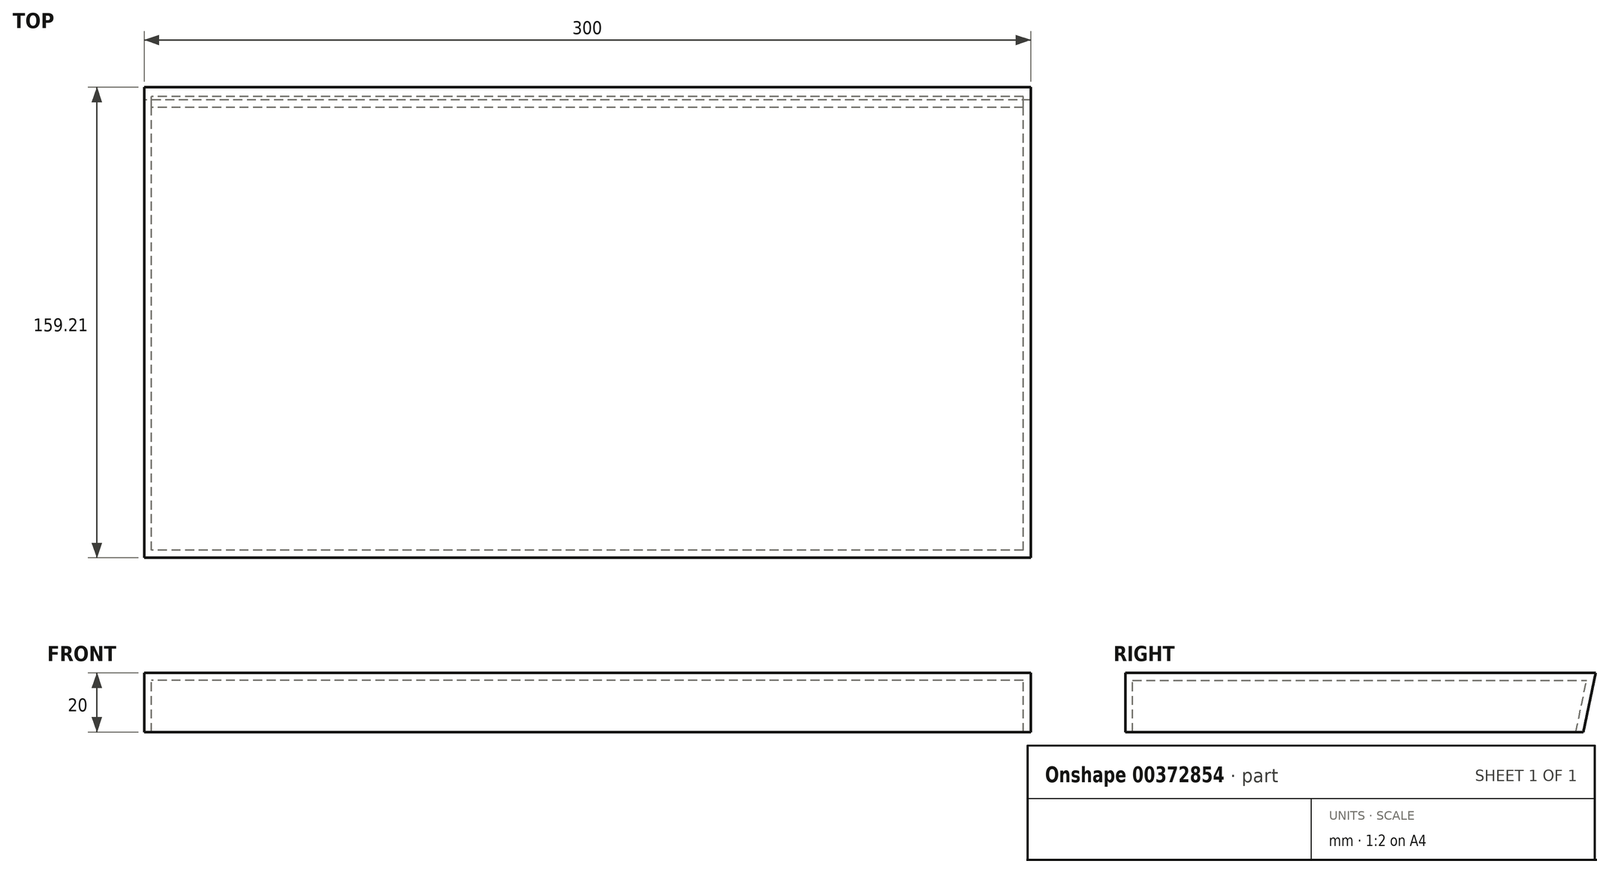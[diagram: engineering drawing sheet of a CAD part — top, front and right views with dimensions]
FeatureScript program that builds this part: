
annotation { "Feature Type Name" : "Feature", "Feature Type Description" : "" }
export const myFeature = defineFeature(function(context is Context, id is Id, definition is map)
    precondition{}
    {
        {
            var Q0;
            Q0=qCreatedBy(makeId("Right.planeOp"),FACE);
            var sketch = newSketch(context, id + "F0", { "sketchPlane" : qUnion([Q0])});
            skLineSegment(sketch, "E0", {"start": v(0, 0) * mm, "end": v(155, 0) * mm});
            skLineSegment(sketch, "E1", {"start": v(0, 0) * mm, "end": v(0, 20) * mm});
            skLineSegment(sketch, "E2", {"start": v(0, 20) * mm, "end": v(155, 20) * mm});
            skLineSegment(sketch, "E3", {"start": v(155, 0) * mm, "end": v(159.2, 20) * mm});
            skLineSegment(sketch, "E4", {"start": v(155, 20) * mm, "end": v(159.2, 20) * mm});
            skSolve(sketch);
        }
        {
            var Q0;
            Q0 = qSketchRegion(id + "F0", true);
            extrude(context, id + "F1", {"entities" : qUnion([Q0]), "depth" : 300 * mm});
        }
        {
            var Q0;
            Q0=makeQuery(id+"F1.opExtrude","SWEPT_FACE",FACE,{"disambiguationData":[OSD([sQuery(id+"F0.wireOp",EDGE,"E0")])]});
            shell(context, id + "F2", {"entities" : qUnion([Q0]), "thickness" : 2.5 * mm});
        }
    });
